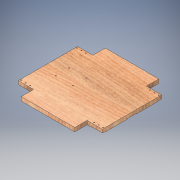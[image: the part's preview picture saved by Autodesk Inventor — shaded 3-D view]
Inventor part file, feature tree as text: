
AUTODESK INVENTOR PART (.ipt)
format: ipt  version: 2017 (Build 210142000, 142)  size: 217,600 bytes
history: native  units: in
note: dims shown in document units (in); Inventor stores cm internally (conversion verified against a paired STEP export)
features: extrude x2, sketch x2
ambient origin geometry x8: Origin, YZ Plane, XZ Plane, XY Plane, X Axis, Y Axis, Z Axis, Center Point
bodies: Solid1 (feature_tree)
feature tree (4):
  extrude  "Extrusion1"  Depth=0.0625in TaperAngle=0.0deg
  extrude  "Extrusion2"  [1 undecoded]
  sketch  "Sketch1"  dims[d1=0.7874in d3=0.7874in d4=11.0in d5=11.0in d6=2.0in d7=1.625in d8=2.0in d9=1.625in d10=2.0in d11=1.625in d12=1.625in d13=5.0in d14=1.25in d15=1.5in d16=0.5in d17=0.125in d18=7.299in d19=9.551in d20=0.5in d21=0.0in]
  sketch  "Sketch3"  dims[d23=0.7874in d25=0.7874in d26=11.0in d27=11.0in d30=2.0in d31=1.625in d32=2.0in d33=1.625in d34=1.625in d35=5.0in d36=1.25in d37=1.5in d38=0.5in d39=0.125in d40=7.299in d41=9.551in d42=0.0625in d43=0.0in]
note: 1 required parameter value undecoded (feature->parameter linkage not recoverable at this tier; creation-order binding heuristic only, values carry confidence <= 0.55)
